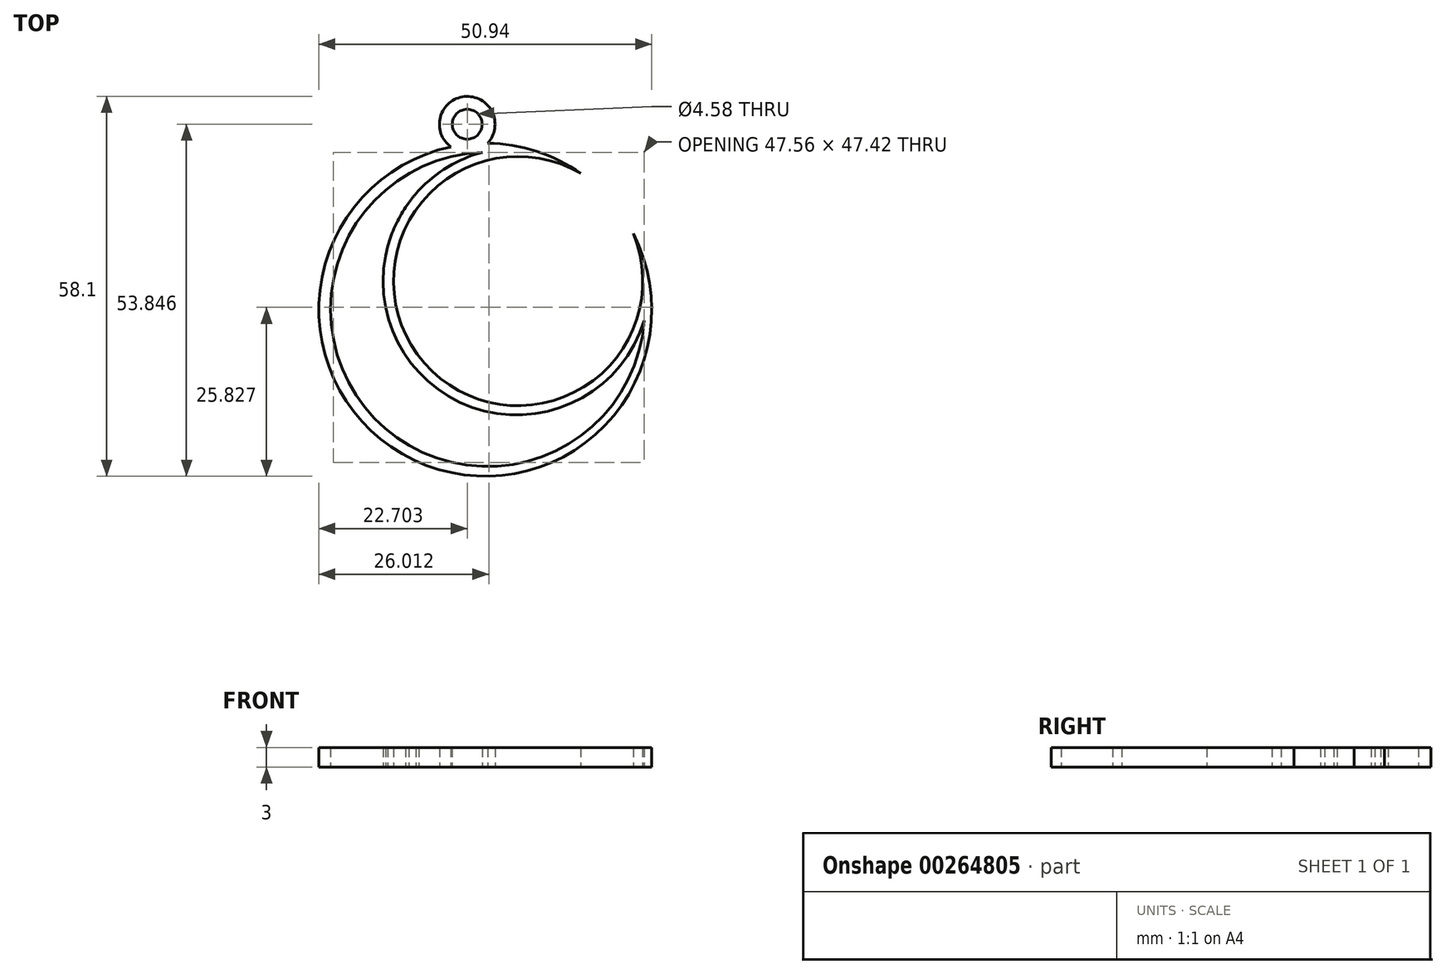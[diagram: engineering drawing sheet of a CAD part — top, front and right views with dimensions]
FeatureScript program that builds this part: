
annotation { "Feature Type Name" : "Feature", "Feature Type Description" : "" }
export const myFeature = defineFeature(function(context is Context, id is Id, definition is map)
    precondition{}
    {
        {
            var Q0;
            Q0=qCreatedBy(makeId("Top.planeOp"),FACE);
            var sketch = newSketch(context, id + "F0", { "sketchPlane" : qUnion([Q0])});
            skArc(sketch, "E0", {"start": v(9.59, 16.48) * mm, "mid": v(-24.2, -21.13) * mm, "end": v(17.62, 7.27) * mm});
            skArc(sketch, "E1", {"start": v(9.59, 16.48) * mm, "mid": v(-14.36, -12.54) * mm, "end": v(17.62, 7.27) * mm});
            skArc(sketch, "E2", {"start": v(-5.5, 19.69) * mm, "mid": v(-21.97, -21) * mm, "end": v(19.3, -6.06) * mm});
            skArc(sketch, "E3", {"start": v(-5.5, 19.69) * mm, "mid": v(-14.94, -14.23) * mm, "end": v(19.3, -6.06) * mm});
            skCircle(sketch, "E4", {"center": v(-7.79, 24) * mm, "radius": 4.26 * mm});
            skCircle(sketch, "E5", {"center": v(-7.79, 24) * mm, "radius": 2.3 * mm});
            skLineSegment(sketch, "E6", {"start": v(-5.5, 23.76) * mm, "end": v(-3.53, 23.76) * mm, "construction": true});
            skLineSegment(sketch, "E7", {"start": v(-20.28, 3.87) * mm, "end": v(-19.94, 5.33) * mm});
            skPoint(sketch, "E8.endSnap0", {"position": v(-17.2, 14.17) * mm});
            skLineSegment(sketch, "E9", {"start": v(-17.2, 11.3) * mm, "end": v(-16.74, 11.98) * mm});
            skLineSegment(sketch, "E10", {"start": v(-15.18, 13.87) * mm, "end": v(-15.62, 13.38) * mm});
            skSolve(sketch);
        }
        {
            var Q0;
            Q0=makeQuery(id+"F0.imprint","IMPRINT",FACE,{"disambiguationData":[TD([[makeQuery(id+"F0.imprint","IMPRINT",EDGE,{"derivedFrom":sQuery(id+"F0.wireOp",EDGE,"E5")}),-1.0]])]});
            var Q1;
            {var subQ0=sQuery(id+"F0.wireOp",EDGE,"E4");var subQ1=sQuery(id+"F0.wireOp",EDGE,"E0");var subQ2=makeQuery(id+"F0.imprint","INTERSECT",VERTEX,{"disambiguationData":[OD(0.0)],"derivedFrom":[subQ1,subQ0]});Q1=makeQuery(id+"F0.imprint","IMPRINT",FACE,{"disambiguationData":[TD([[makeQuery(id+"F0.imprint","IMPRINT",EDGE,{"disambiguationData":[TD([[subQ2,-1.0]])],"derivedFrom":subQ1}),1.0]])]});}
            var Q2;
            {var subQ9=sQuery(id+"F0.wireOp",EDGE,"E1");Q2=makeQuery(id+"F0.imprint","IMPRINT",FACE,{"disambiguationData":[TD([[makeQuery(id+"F0.imprint","IMPRINT",EDGE,{"derivedFrom":subQ9}),-1.0]])]});}
            extrude(context, id + "F1", {"entities" : qUnion([Q0, Q1, Q2]), "depth" : 3 * mm, "offsetDistance" : 25 * mm});
        }
    });
